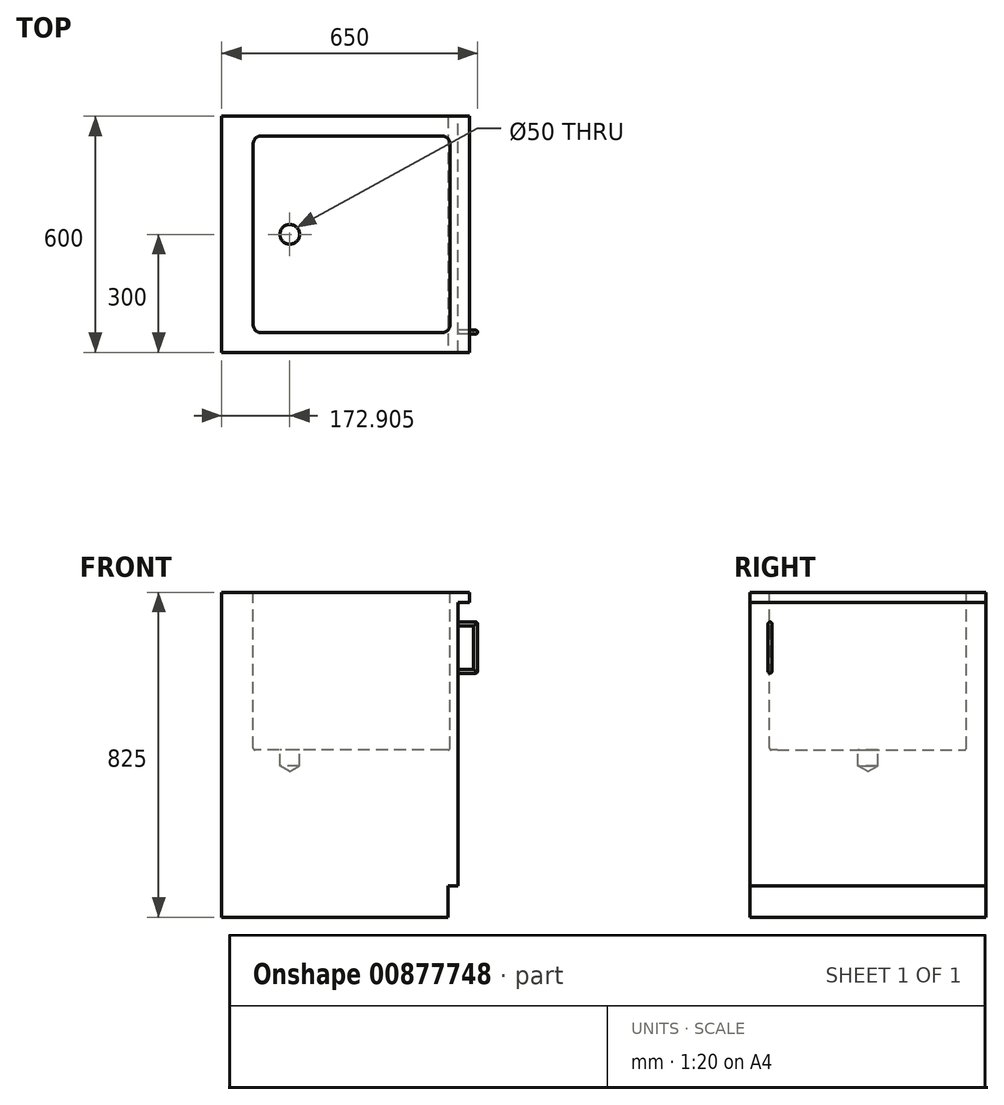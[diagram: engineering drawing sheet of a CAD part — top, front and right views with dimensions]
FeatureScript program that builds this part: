
annotation { "Feature Type Name" : "Feature", "Feature Type Description" : "" }
export const myFeature = defineFeature(function(context is Context, id is Id, definition is map)
    precondition{}
    {
        {
            var Q0;
            Q0=qCreatedBy(makeId("Top.planeOp"),FACE);
            var sketch = newSketch(context, id + "F0", { "sketchPlane" : qUnion([Q0])});
            skLineSegment(sketch, "E0.bottom", {"start": v(-300, 300) * mm, "end": v(300, 300) * mm});
            skLineSegment(sketch, "E0.top", {"start": v(-300, -300) * mm, "end": v(300, -300) * mm});
            skLineSegment(sketch, "E0.left", {"start": v(-300, 300) * mm, "end": v(-300, -300) * mm});
            skLineSegment(sketch, "E0.right", {"start": v(300, 300) * mm, "end": v(300, -300) * mm});
            skPoint(sketch, "E0.middle", {"position": v(0, 0) * mm});
            skSolve(sketch);
        }
        {
            var Q0;
            Q0=qSketchRegion(id+"F0",true);
            extrude(context, id + "F1", {"entities" : qUnion([Q0]), "depth" : 800 * mm, "offsetDistance" : 25 * mm});
        }
        {
            var Q0;
            Q0=makeQuery(id+"F1.opExtrude","SWEPT_FACE",FACE,{"disambiguationData":[OSD([sQuery(id+"F0.wireOp",EDGE,"E0.right")])]});
            var sketch = newSketch(context, id + "F2", { "sketchPlane" : qUnion([Q0])});
            skLineSegment(sketch, "E1.bottom", {"start": v(-300, 0) * mm, "end": v(300, 0) * mm});
            skLineSegment(sketch, "E1.top", {"start": v(-300, 80) * mm, "end": v(300, 80) * mm});
            skLineSegment(sketch, "E1.left", {"start": v(-300, 0) * mm, "end": v(-300, 80) * mm});
            skLineSegment(sketch, "E1.right", {"start": v(300, 0) * mm, "end": v(300, 80) * mm});
            skSolve(sketch);
        }
        {
            var Q0;
            Q0=qSketchRegion(id+"F2",true);
            extrude(context, id + "F3", {"entities" : qUnion([Q0]), "operationType" : NewBodyOperationType.REMOVE, "oppositeDirection" : true, "depth" : 25 * mm, "offsetDistance" : 25 * mm});
        }
        {
            var Q0;
            Q0=makeQuery(id+"F1.opExtrude","SWEPT_FACE",FACE,{"disambiguationData":[OSD([sQuery(id+"F0.wireOp",EDGE,"E0.right")])]});
            var sketch = newSketch(context, id + "F4", { "sketchPlane" : qUnion([Q0])});
            skLineSegment(sketch, "E2.bottom", {"start": v(-248.58, 750) * mm, "end": v(-248.58, 750) * mm});
            skLineSegment(sketch, "E2.top", {"start": v(-248.58, 620) * mm, "end": v(-248.58, 620) * mm});
            skLineSegment(sketch, "E2.left", {"start": v(-253.58, 745) * mm, "end": v(-253.58, 625) * mm});
            skLineSegment(sketch, "E2.right", {"start": v(-243.58, 745) * mm, "end": v(-243.58, 625) * mm});
            skPoint(sketch, "E3.visualSharp", {"position": v(-243.58, 750) * mm});
            skArc(sketch, "E3.filletArc", {"start": v(-243.58, 745) * mm, "mid": v(-245.04, 748.54) * mm, "end": v(-248.58, 750) * mm});
            skPoint(sketch, "E4.visualSharp", {"position": v(-243.58, 620) * mm});
            skArc(sketch, "E4.filletArc", {"start": v(-248.58, 620) * mm, "mid": v(-245.04, 621.46) * mm, "end": v(-243.58, 625) * mm});
            skPoint(sketch, "E5.visualSharp", {"position": v(-253.58, 620) * mm});
            skArc(sketch, "E5.filletArc", {"start": v(-253.58, 625) * mm, "mid": v(-252.12, 621.46) * mm, "end": v(-248.58, 620) * mm});
            skPoint(sketch, "E6.visualSharp", {"position": v(-253.58, 750) * mm});
            skArc(sketch, "E6.filletArc", {"start": v(-248.58, 750) * mm, "mid": v(-252.12, 748.54) * mm, "end": v(-253.58, 745) * mm});
            skSolve(sketch);
        }
        {
            var Q0;
            Q0=qSketchRegion(id+"F4",true);
            extrude(context, id + "F5", {"entities" : qUnion([Q0]), "operationType" : NewBodyOperationType.ADD, "depth" : 50 * mm, "offsetDistance" : 25 * mm});
        }
        {
            var Q0;
            Q0=makeQuery(id+"F5.opExtrude","CAP_FACE",FACE,{"disambiguationData":[OSD([sQuery(id+"F4.wireOp",EDGE,"E2.left"),sQuery(id+"F4.wireOp",EDGE,"E2.right"),sQuery(id+"F4.wireOp",EDGE,"E3.filletArc"),sQuery(id+"F4.wireOp",EDGE,"E4.filletArc"),sQuery(id+"F4.wireOp",EDGE,"E5.filletArc"),sQuery(id+"F4.wireOp",EDGE,"E6.filletArc")])],"isStart":false});
            fillet(context, id + "F6", {"entities" : qUnion([Q0]), "radius" : 5 * mm, "tangentPropagation" : true, "allowEdgeOverflow" : false});
        }
        {
            var Q0;
            Q0=makeQuery(id+"F5.opExtrude","SWEPT_FACE",FACE,{"disambiguationData":[OSD([sQuery(id+"F4.wireOp",EDGE,"E2.right")])]});
            var sketch = newSketch(context, id + "F7", { "sketchPlane" : qUnion([Q0])});
            skLineSegment(sketch, "E7.bottom", {"start": v(-340, 740) * mm, "end": v(-300, 740) * mm});
            skLineSegment(sketch, "E7.top", {"start": v(-340, 630) * mm, "end": v(-300, 630) * mm});
            skLineSegment(sketch, "E7.left", {"start": v(-340, 740) * mm, "end": v(-340, 630) * mm});
            skLineSegment(sketch, "E7.right", {"start": v(-300, 740) * mm, "end": v(-300, 630) * mm});
            skSolve(sketch);
        }
        {
            var Q0;
            Q0=makeQuery(id+"F7.imprint","IMPRINT",FACE,{"disambiguationData":[TD([[makeQuery(id+"F7.imprint","IMPRINT",EDGE,{"derivedFrom":sQuery(id+"F7.wireOp",EDGE,"E7.bottom")}),-1.0]])]});
            extrude(context, id + "F8", {"entities" : qUnion([Q0]), "operationType" : NewBodyOperationType.REMOVE, "oppositeDirection" : true, "depth" : 25 * mm, "offsetDistance" : 25 * mm});
        }
        {
            var Q0;
            Q0=makeQuery(id+"F8.boolean.opBoolean","COPY",EDGE,{"derivedFrom":makeQuery(id+"F8.opExtrude","CAP_EDGE",EDGE,{"disambiguationData":[OSD([sQuery(id+"F7.wireOp",EDGE,"E7.bottom")])],"isStart":true})});
            var Q1;
            Q1=makeQuery(id+"F8.boolean.opBoolean","COPY",EDGE,{"derivedFrom":makeQuery(id+"F8.opExtrude","CAP_EDGE",EDGE,{"disambiguationData":[OSD([sQuery(id+"F7.wireOp",EDGE,"E7.left")])],"isStart":true})});
            var Q2;
            Q2=makeQuery(id+"F8.boolean.opBoolean","COPY",EDGE,{"derivedFrom":makeQuery(id+"F8.opExtrude","CAP_EDGE",EDGE,{"disambiguationData":[OSD([sQuery(id+"F7.wireOp",EDGE,"E7.top")])],"isStart":true})});
            var Q3;
            Q3=makeQuery(id+"F8.boolean.opBoolean","INTERSECT",EDGE,{"derivedFrom":[makeQuery(id+"F5.opExtrude","SWEPT_FACE",FACE,{"disambiguationData":[OSD([sQuery(id+"F4.wireOp",EDGE,"E2.left")])]}),makeQuery(id+"F8.opExtrude","SWEPT_FACE",FACE,{"disambiguationData":[OSD([sQuery(id+"F7.wireOp",EDGE,"E7.bottom")])]})]});
            var Q4;
            Q4=makeQuery(id+"F8.boolean.opBoolean","INTERSECT",EDGE,{"derivedFrom":[makeQuery(id+"F5.opExtrude","SWEPT_FACE",FACE,{"disambiguationData":[OSD([sQuery(id+"F4.wireOp",EDGE,"E2.left")])]}),makeQuery(id+"F8.opExtrude","SWEPT_FACE",FACE,{"disambiguationData":[OSD([sQuery(id+"F7.wireOp",EDGE,"E7.left")])]})]});
            var Q5;
            Q5=makeQuery(id+"F8.boolean.opBoolean","INTERSECT",EDGE,{"derivedFrom":[makeQuery(id+"F5.opExtrude","SWEPT_FACE",FACE,{"disambiguationData":[OSD([sQuery(id+"F4.wireOp",EDGE,"E2.left")])]}),makeQuery(id+"F8.opExtrude","SWEPT_FACE",FACE,{"disambiguationData":[OSD([sQuery(id+"F7.wireOp",EDGE,"E7.top")])]})]});
            fillet(context, id + "F9", {"entities" : qUnion([Q0, Q1, Q2, Q3, Q4, Q5]), "radius" : 5 * mm, "tangentPropagation" : true, "allowEdgeOverflow" : false});
        }
        {
            var Q0;
            Q0=makeQuery(id+"F1.opExtrude","CAP_FACE",FACE,{"disambiguationData":[OSD([sQuery(id+"F0.wireOp",EDGE,"E0.bottom"),sQuery(id+"F0.wireOp",EDGE,"E0.top"),sQuery(id+"F0.wireOp",EDGE,"E0.left"),sQuery(id+"F0.wireOp",EDGE,"E0.right")])],"isStart":false});
            var sketch = newSketch(context, id + "F10", { "sketchPlane" : qUnion([Q0])});
            skLineSegment(sketch, "E8.bottom", {"start": v(-300, -300) * mm, "end": v(330, -300) * mm});
            skLineSegment(sketch, "E8.top", {"start": v(-300, 300) * mm, "end": v(330, 300) * mm});
            skLineSegment(sketch, "E8.left", {"start": v(-300, -300) * mm, "end": v(-300, 300) * mm});
            skLineSegment(sketch, "E8.right", {"start": v(330, -300) * mm, "end": v(330, 300) * mm});
            skSolve(sketch);
        }
        {
            var Q0;
            Q0=qSketchRegion(id+"F10",true);
            extrude(context, id + "F11", {"entities" : qUnion([Q0]), "operationType" : NewBodyOperationType.ADD, "depth" : 25 * mm, "offsetDistance" : 25 * mm});
        }
        {
            var Q0;
            Q0=makeQuery(id+"F11.opExtrude","CAP_FACE",FACE,{"disambiguationData":[OSD([sQuery(id+"F10.wireOp",EDGE,"E8.bottom"),sQuery(id+"F10.wireOp",EDGE,"E8.top"),sQuery(id+"F10.wireOp",EDGE,"E8.left"),sQuery(id+"F10.wireOp",EDGE,"E8.right")])],"isStart":false});
            var sketch = newSketch(context, id + "F12", { "sketchPlane" : qUnion([Q0])});
            skLineSegment(sketch, "E9.bottom", {"start": v(260, -250) * mm, "end": v(-200, -250) * mm});
            skLineSegment(sketch, "E9.top", {"start": v(260, 250) * mm, "end": v(-200, 250) * mm});
            skLineSegment(sketch, "E9.left", {"start": v(280, -230) * mm, "end": v(280, 230) * mm});
            skLineSegment(sketch, "E9.right", {"start": v(-220, -230) * mm, "end": v(-220, 230) * mm});
            skPoint(sketch, "E10.visualSharp", {"position": v(-220, -250) * mm});
            skArc(sketch, "E10.filletArc", {"start": v(-220, -230) * mm, "mid": v(-214.14, -244.14) * mm, "end": v(-200, -250) * mm});
            skPoint(sketch, "E11.visualSharp", {"position": v(-220, 250) * mm});
            skArc(sketch, "E11.filletArc", {"start": v(-200, 250) * mm, "mid": v(-214.14, 244.14) * mm, "end": v(-220, 230) * mm});
            skPoint(sketch, "E12.visualSharp", {"position": v(280, 250) * mm});
            skArc(sketch, "E12.filletArc", {"start": v(280, 230) * mm, "mid": v(274.14, 244.14) * mm, "end": v(260, 250) * mm});
            skPoint(sketch, "E13.visualSharp", {"position": v(280, -250) * mm});
            skArc(sketch, "E13.filletArc", {"start": v(260, -250) * mm, "mid": v(274.14, -244.14) * mm, "end": v(280, -230) * mm});
            skSolve(sketch);
        }
        {
            var Q0;
            Q0=qSketchRegion(id+"F12",true);
            extrude(context, id + "F13", {"entities" : qUnion([Q0]), "operationType" : NewBodyOperationType.REMOVE, "oppositeDirection" : true, "depth" : 400 * mm, "offsetDistance" : 25 * mm});
        }
        {
            var Q0;
            Q0=makeQuery(id+"F13.boolean.opBoolean","COPY",EDGE,{"derivedFrom":makeQuery(id+"F13.opExtrude","CAP_EDGE",EDGE,{"disambiguationData":[OSD([sQuery(id+"F12.wireOp",EDGE,"E9.top")])],"isStart":false})});
            var Q1;
            Q1=makeQuery(id+"F13.boolean.opBoolean","COPY",EDGE,{"derivedFrom":makeQuery(id+"F13.opExtrude","CAP_EDGE",EDGE,{"disambiguationData":[OSD([sQuery(id+"F12.wireOp",EDGE,"E11.filletArc")])],"isStart":false})});
            var Q2;
            Q2=makeQuery(id+"F13.boolean.opBoolean","COPY",EDGE,{"derivedFrom":makeQuery(id+"F13.opExtrude","CAP_EDGE",EDGE,{"disambiguationData":[OSD([sQuery(id+"F12.wireOp",EDGE,"E9.right")])],"isStart":false})});
            var Q3;
            Q3=makeQuery(id+"F13.boolean.opBoolean","COPY",FACE,{"derivedFrom":makeQuery(id+"F13.opExtrude","CAP_FACE",FACE,{"disambiguationData":[OSD([sQuery(id+"F12.wireOp",EDGE,"E9.bottom"),sQuery(id+"F12.wireOp",EDGE,"E9.top"),sQuery(id+"F12.wireOp",EDGE,"E9.left"),sQuery(id+"F12.wireOp",EDGE,"E9.right"),sQuery(id+"F12.wireOp",EDGE,"E10.filletArc"),sQuery(id+"F12.wireOp",EDGE,"E11.filletArc"),sQuery(id+"F12.wireOp",EDGE,"E12.filletArc"),sQuery(id+"F12.wireOp",EDGE,"E13.filletArc")])],"isStart":false})});
            fillet(context, id + "F14", {"entities" : qUnion([Q0, Q1, Q2, Q3]), "radius" : 5 * mm, "tangentPropagation" : true, "allowEdgeOverflow" : false});
        }
        {
            var Q0;
            Q0=makeQuery(id+"F13.boolean.opBoolean","COPY",FACE,{"derivedFrom":makeQuery(id+"F13.opExtrude","CAP_FACE",FACE,{"disambiguationData":[OSD([sQuery(id+"F12.wireOp",EDGE,"E9.bottom"),sQuery(id+"F12.wireOp",EDGE,"E9.top"),sQuery(id+"F12.wireOp",EDGE,"E9.left"),sQuery(id+"F12.wireOp",EDGE,"E9.right"),sQuery(id+"F12.wireOp",EDGE,"E10.filletArc"),sQuery(id+"F12.wireOp",EDGE,"E11.filletArc"),sQuery(id+"F12.wireOp",EDGE,"E12.filletArc"),sQuery(id+"F12.wireOp",EDGE,"E13.filletArc")])],"isStart":false})});
            var sketch = newSketch(context, id + "F15", { "sketchPlane" : qUnion([Q0])});
            skPoint(sketch, "E14", {"position": v(-127.1, 0) * mm});
            skSolve(sketch);
        }
        {
            var Q0;
            Q0=sQuery(id+"F15.wireOp",VERTEX,"E14");
            var Q1;
            Q1=makeQuery(id+"F1.opExtrude","SWEPT_BODY",BODY,{"disambiguationData":[OSD([sQuery(id+"F0.wireOp",EDGE,"E0.bottom"),sQuery(id+"F0.wireOp",EDGE,"E0.top"),sQuery(id+"F0.wireOp",EDGE,"E0.left"),sQuery(id+"F0.wireOp",EDGE,"E0.right")])]});
            hole(context, id + "F16", {"style" : HoleStyle.SIMPLE, "endStyle" : HoleEndStyle.BLIND, "holeDiameter" : 50 * mm, "majorDiameter" : 5 * mm, "holeDepth" : 40 * mm, "isTappedThrough" : true, "tappedDepth" : 12 * mm, "tapClearance" : 3, "locations" : qUnion([Q0]), "scope" : qUnion([Q1])});
        }
    });
